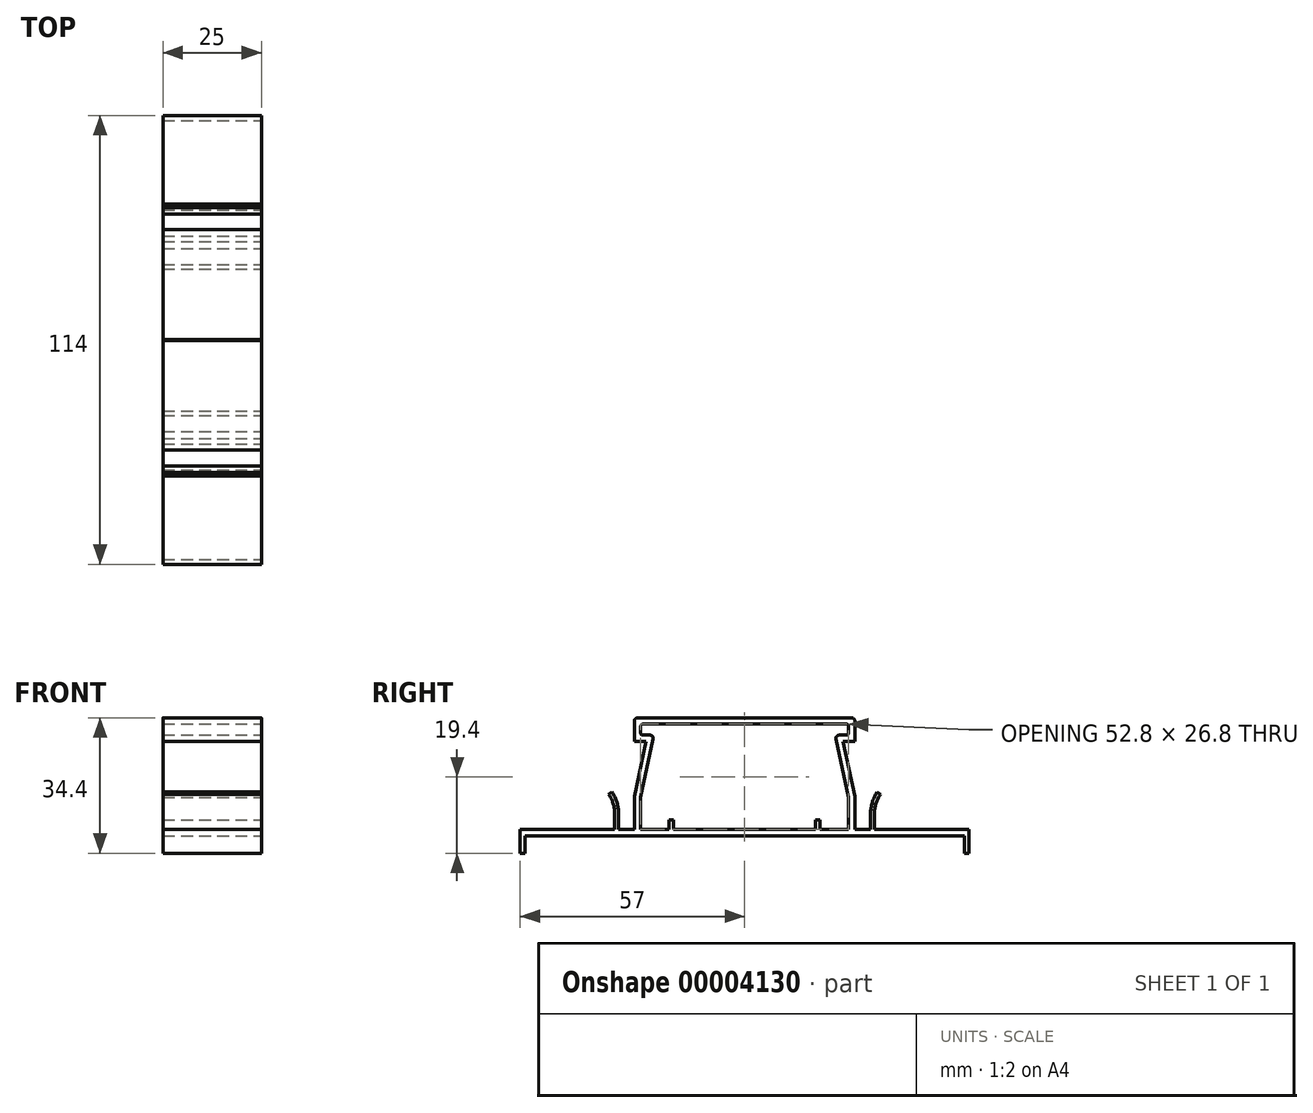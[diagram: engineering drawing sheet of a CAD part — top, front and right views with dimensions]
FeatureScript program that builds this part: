
annotation { "Feature Type Name" : "Feature", "Feature Type Description" : "" }
export const myFeature = defineFeature(function(context is Context, id is Id, definition is map)
    precondition{}
    {
        {
            var Q0;
            Q0=qCreatedBy(makeId("Right.planeOp"),FACE);
            var sketch = newSketch(context, id + "F0", { "sketchPlane" : qUnion([Q0])});
            skLineSegment(sketch, "E0", {"start": v(57, 0) * mm, "end": v(57, -6) * mm});
            skLineSegment(sketch, "E1", {"start": v(57, -6) * mm, "end": v(55.8, -6) * mm});
            skLineSegment(sketch, "E2", {"start": v(55.8, -6) * mm, "end": v(55.8, -1.6) * mm});
            skLineSegment(sketch, "E3", {"start": v(55.8, -1.6) * mm, "end": v(0, -1.6) * mm});
            skLineSegment(sketch, "E4", {"start": v(28, 8.4) * mm, "end": v(25, 22.4) * mm});
            skLineSegment(sketch, "E5", {"start": v(25, 22.4) * mm, "end": v(28, 22.4) * mm});
            skLineSegment(sketch, "E6", {"start": v(28, 22.4) * mm, "end": v(28, 28.4) * mm});
            skLineSegment(sketch, "E7", {"start": v(28, 28.4) * mm, "end": v(0, 28.4) * mm});
            skLineSegment(sketch, "E8", {"start": v(57, 0) * mm, "end": v(28, 0) * mm});
            skLineSegment(sketch, "E9", {"start": v(28, 0) * mm, "end": v(0, 0) * mm});
            skLineSegment(sketch, "E10", {"start": v(28, 8.4) * mm, "end": v(28, 0) * mm});
            skLineSegment(sketch, "E11", {"start": v(0, 28.4) * mm, "end": v(0, 28.3) * mm});
            skLineSegment(sketch, "E12", {"start": v(18, 0) * mm, "end": v(18, 2.5) * mm});
            skLineSegment(sketch, "E13", {"start": v(18, 2.5) * mm, "end": v(19.2, 2.5) * mm});
            skLineSegment(sketch, "E14", {"start": v(19.2, 2.5) * mm, "end": v(19.2, 0) * mm});
            skLineSegment(sketch, "E15", {"start": v(33, 0) * mm, "end": v(33, 4) * mm});
            skArc(sketch, "E16", {"start": v(33, 4) * mm, "mid": v(33.39, 6.61) * mm, "end": v(34.52, 9) * mm});
            skArc(sketch, "E17.0", {"start": v(32, 4) * mm, "mid": v(32.43, 6.9) * mm, "end": v(33.69, 9.56) * mm});
            skLineSegment(sketch, "E17.1", {"start": v(32, 0) * mm, "end": v(32, 4) * mm});
            skLineSegment(sketch, "E18", {"start": v(33.69, 9.56) * mm, "end": v(34.52, 9) * mm});
            skLineSegment(sketch, "E19.0.MirrorCS", {"start": v(-55.8, -6) * mm, "end": v(-55.8, -1.6) * mm});
            skLineSegment(sketch, "E19.1.MirrorCS", {"start": v(-57, -6) * mm, "end": v(-55.8, -6) * mm});
            skLineSegment(sketch, "E19.2.MirrorCS", {"start": v(-57, 0) * mm, "end": v(-57, -6) * mm});
            skLineSegment(sketch, "E19.3.MirrorCS", {"start": v(-33, 0) * mm, "end": v(-33, 4) * mm});
            skArc(sketch, "E19.4.MirrorCS", {"start": v(-33, 4) * mm, "mid": v(-33.39, 6.61) * mm, "end": v(-34.52, 9) * mm});
            skLineSegment(sketch, "E19.5.MirrorCS", {"start": v(-33.69, 9.56) * mm, "end": v(-34.52, 9) * mm});
            skArc(sketch, "E19.6.MirrorCS", {"start": v(-32, 4) * mm, "mid": v(-32.43, 6.9) * mm, "end": v(-33.69, 9.56) * mm});
            skLineSegment(sketch, "E19.7.MirrorCS", {"start": v(-32, 0) * mm, "end": v(-32, 4) * mm});
            skLineSegment(sketch, "E19.8.MirrorCS", {"start": v(-57, 0) * mm, "end": v(-28, 0) * mm});
            skLineSegment(sketch, "E19.9.MirrorCS", {"start": v(-55.8, -1.6) * mm, "end": v(0, -1.6) * mm});
            skLineSegment(sketch, "E19.10.MirrorCS", {"start": v(-19.2, 2.5) * mm, "end": v(-19.2, 0) * mm});
            skLineSegment(sketch, "E19.11.MirrorCS", {"start": v(-18, 2.5) * mm, "end": v(-19.2, 2.5) * mm});
            skLineSegment(sketch, "E19.12.MirrorCS", {"start": v(-18, 0) * mm, "end": v(-18, 2.5) * mm});
            skLineSegment(sketch, "E19.13.MirrorCS", {"start": v(-28, 0) * mm, "end": v(0, 0) * mm});
            skLineSegment(sketch, "E19.14.MirrorCS", {"start": v(-28, 8.4) * mm, "end": v(-28, 0) * mm});
            skLineSegment(sketch, "E19.15.MirrorCS", {"start": v(-28, 8.4) * mm, "end": v(-25, 22.4) * mm});
            skLineSegment(sketch, "E19.16.MirrorCS", {"start": v(-25, 22.4) * mm, "end": v(-28, 22.4) * mm});
            skLineSegment(sketch, "E19.17.MirrorCS", {"start": v(-28, 28.4) * mm, "end": v(0, 28.4) * mm});
            skLineSegment(sketch, "E19.18.MirrorCS", {"start": v(-28, 22.4) * mm, "end": v(-28, 28.4) * mm});
            skLineSegment(sketch, "E20.0", {"start": v(-26.4, 26.8) * mm, "end": v(0, 26.8) * mm});
            skLineSegment(sketch, "E20.1", {"start": v(-26.4, 24) * mm, "end": v(-26.4, 26.8) * mm});
            skLineSegment(sketch, "E20.2", {"start": v(-23.02, 24) * mm, "end": v(-26.4, 24) * mm});
            skLineSegment(sketch, "E20.3", {"start": v(-26.4, 8.23) * mm, "end": v(-23.02, 24) * mm});
            skLineSegment(sketch, "E20.4", {"start": v(-26.4, 8.23) * mm, "end": v(-26.4, 0) * mm});
            skLineSegment(sketch, "E21.0", {"start": v(26.4, 26.8) * mm, "end": v(0, 26.8) * mm});
            skLineSegment(sketch, "E21.1", {"start": v(26.4, 24) * mm, "end": v(26.4, 26.8) * mm});
            skLineSegment(sketch, "E21.2", {"start": v(23.02, 24) * mm, "end": v(26.4, 24) * mm});
            skLineSegment(sketch, "E21.3", {"start": v(26.4, 8.23) * mm, "end": v(23.02, 24) * mm});
            skLineSegment(sketch, "E21.4", {"start": v(26.4, 8.23) * mm, "end": v(26.4, 0) * mm});
            skSolve(sketch);
        }
        {
            var Q0;
            {var subQ16=sQuery(id+"F0.wireOp",EDGE,"E0");Q0=makeQuery(id+"F0.imprint","IMPRINT",FACE,{"disambiguationData":[TD([[makeQuery(id+"F0.imprint","IMPRINT",EDGE,{"derivedFrom":subQ16}),-1.0]])]});}
            var Q1;
            Q1=makeQuery(id+"F0.imprint","IMPRINT",FACE,{"disambiguationData":[TD([[makeQuery(id+"F0.imprint","IMPRINT",EDGE,{"derivedFrom":sQuery(id+"F0.wireOp",EDGE,"E4")}),1.0]])]});
            var Q2;
            {var subQ2=sQuery(id+"F0.wireOp",EDGE,"E19.3.MirrorCS");Q2=makeQuery(id+"F0.imprint","IMPRINT",FACE,{"disambiguationData":[TD([[makeQuery(id+"F0.imprint","IMPRINT",EDGE,{"derivedFrom":subQ2}),-1.0]])]});}
            var Q3;
            {var subQ1=sQuery(id+"F0.wireOp",EDGE,"E15");Q3=makeQuery(id+"F0.imprint","IMPRINT",FACE,{"disambiguationData":[TD([[makeQuery(id+"F0.imprint","IMPRINT",EDGE,{"derivedFrom":subQ1}),1.0]])]});}
            var Q4;
            {var subQ1=sQuery(id+"F0.wireOp",EDGE,"E12");Q4=makeQuery(id+"F0.imprint","IMPRINT",FACE,{"disambiguationData":[TD([[makeQuery(id+"F0.imprint","IMPRINT",EDGE,{"derivedFrom":subQ1}),-1.0]])]});}
            var Q5;
            {var subQ2=sQuery(id+"F0.wireOp",EDGE,"E19.10.MirrorCS");Q5=makeQuery(id+"F0.imprint","IMPRINT",FACE,{"disambiguationData":[TD([[makeQuery(id+"F0.imprint","IMPRINT",EDGE,{"derivedFrom":subQ2}),1.0]])]});}
            extrude(context, id + "F1", {"entities" : qUnion([Q0, Q1, Q2, Q3, Q4, Q5]), "oppositeDirection" : true, "depth" : 25 * mm});
        }
        {
            var Q0;
            Q0=makeQuery(id+"F1.opExtrude","SWEPT_EDGE",EDGE,{"disambiguationData":[OSD([sQuery(id+"F0.wireOp",EDGE,"E19.17.MirrorCS"),sQuery(id+"F0.wireOp",EDGE,"E19.18.MirrorCS")])]});
            var Q1;
            Q1=makeQuery(id+"F1.opExtrude","SWEPT_EDGE",EDGE,{"disambiguationData":[OSD([sQuery(id+"F0.wireOp",EDGE,"E6"),sQuery(id+"F0.wireOp",EDGE,"E7")])]});
            var Q2;
            Q2=makeQuery(id+"F1.opExtrude","SWEPT_EDGE",EDGE,{"disambiguationData":[OSD([sQuery(id+"F0.wireOp",EDGE,"E21.2"),sQuery(id+"F0.wireOp",EDGE,"E21.3")])]});
            var Q3;
            Q3=makeQuery(id+"F1.opExtrude","SWEPT_EDGE",EDGE,{"disambiguationData":[OSD([sQuery(id+"F0.wireOp",EDGE,"E20.2"),sQuery(id+"F0.wireOp",EDGE,"E20.3")])]});
            var Q4;
            Q4=makeQuery(id+"F1.opExtrude","SWEPT_EDGE",EDGE,{"disambiguationData":[OSD([sQuery(id+"F0.wireOp",EDGE,"E19.14.MirrorCS"),sQuery(id+"F0.wireOp",EDGE,"E19.15.MirrorCS")])]});
            var Q5;
            Q5=makeQuery(id+"F1.opExtrude","SWEPT_EDGE",EDGE,{"disambiguationData":[OSD([sQuery(id+"F0.wireOp",EDGE,"E4"),sQuery(id+"F0.wireOp",EDGE,"E10")])]});
            fillet(context, id + "F2", {"entities" : qUnion([Q0, Q1, Q2, Q3, Q4, Q5]), "radius" : .8 * mm, "tangentPropagation" : true, "allowEdgeOverflow" : false});
        }
        {
            var Q0;
            Q0=makeQuery(id+"F1.opExtrude","SWEPT_EDGE",EDGE,{"disambiguationData":[OSD([sQuery(id+"F0.wireOp",EDGE,"E20.1"),sQuery(id+"F0.wireOp",EDGE,"E20.2")])]});
            var Q1;
            Q1=makeQuery(id+"F1.opExtrude","SWEPT_EDGE",EDGE,{"disambiguationData":[OSD([sQuery(id+"F0.wireOp",EDGE,"E20.0"),sQuery(id+"F0.wireOp",EDGE,"E20.1")])]});
            var Q2;
            Q2=makeQuery(id+"F1.opExtrude","SWEPT_EDGE",EDGE,{"disambiguationData":[OSD([sQuery(id+"F0.wireOp",EDGE,"E21.0"),sQuery(id+"F0.wireOp",EDGE,"E21.1")])]});
            var Q3;
            Q3=makeQuery(id+"F1.opExtrude","SWEPT_EDGE",EDGE,{"disambiguationData":[OSD([sQuery(id+"F0.wireOp",EDGE,"E21.1"),sQuery(id+"F0.wireOp",EDGE,"E21.2")])]});
            fillet(context, id + "F3", {"entities" : qUnion([Q0, Q1, Q2, Q3]), "radius" : 0.5 * mm, "tangentPropagation" : true, "allowEdgeOverflow" : false});
        }
        {
            var Q0;
            Q0=makeQuery(id+"F1.opExtrude","SWEPT_FACE",FACE,{"disambiguationData":[OSD([sQuery(id+"F0.wireOp",EDGE,"E7"),sQuery(id+"F0.wireOp",EDGE,"E19.17.MirrorCS")])]});
            var sketch = newSketch(context, id + "F4", { "sketchPlane" : qUnion([Q0])});
            skLineSegment(sketch, "E22", {"start": v(-25, 0) * mm, "end": v(0, 0) * mm});
            skLineSegment(sketch, "E23", {"start": v(0, 0.1) * mm, "end": v(-25, 0.1) * mm});
            skLineSegment(sketch, "E24", {"start": v(0, 0.1) * mm, "end": v(-0.03, 0.39) * mm});
            skLineSegment(sketch, "E25", {"start": v(-0.03, 0.39) * mm, "end": v(0, -0.1) * mm});
            skLineSegment(sketch, "E26", {"start": v(-25, -0.1) * mm, "end": v(0, -0.1) * mm});
            skLineSegment(sketch, "E27", {"start": v(-25, -0.1) * mm, "end": v(-25, 0.1) * mm});
            skSolve(sketch);
        }
        {
            var Q0;
            {var subQ1=sQuery(id+"F4.wireOp",EDGE,"E26");Q0=makeQuery(id+"F4.imprint","IMPRINT",FACE,{"disambiguationData":[TD([[makeQuery(id+"F4.imprint","IMPRINT",EDGE,{"derivedFrom":subQ1}),1.0]])]});}
            var Q1;
            {var subQ0=sQuery(id+"F4.wireOp",EDGE,"E27");var subQ5=sQuery(id+"F4.wireOp",EDGE,"E22");var subQ6=makeQuery(id+"F4.imprint","INTERSECT",VERTEX,{"derivedFrom":[subQ5,subQ0]});var subQ7=sQuery(id+"F4.wireOp",EDGE,"E25");var subQ9=makeQuery(id+"F4.imprint","INTERSECT",VERTEX,{"derivedFrom":[subQ5,subQ7]});var subQ10=makeQuery(id+"F4.imprint","IMPRINT",EDGE,{"disambiguationData":[TD([[subQ9,1.0]])],"derivedFrom":subQ7});Q1=qUnion([makeQuery(id+"F4.imprint","IMPRINT",FACE,{"disambiguationData":[TD([[makeQuery(id+"F4.imprint","IMPRINT",EDGE,{"disambiguationData":[TD([[subQ6,-1.0]])],"derivedFrom":subQ5}),1.0]])]}),makeQuery(id+"F4.imprint","IMPRINT",FACE,{"disambiguationData":[TD([[subQ10,1.0]])]})]);}
            extrude(context, id + "F5", {"entities" : qUnion([Q0, Q1]), "operationType" : NewBodyOperationType.REMOVE, "oppositeDirection" : true, "depth" : 0.1 * mm});
        }
    });
